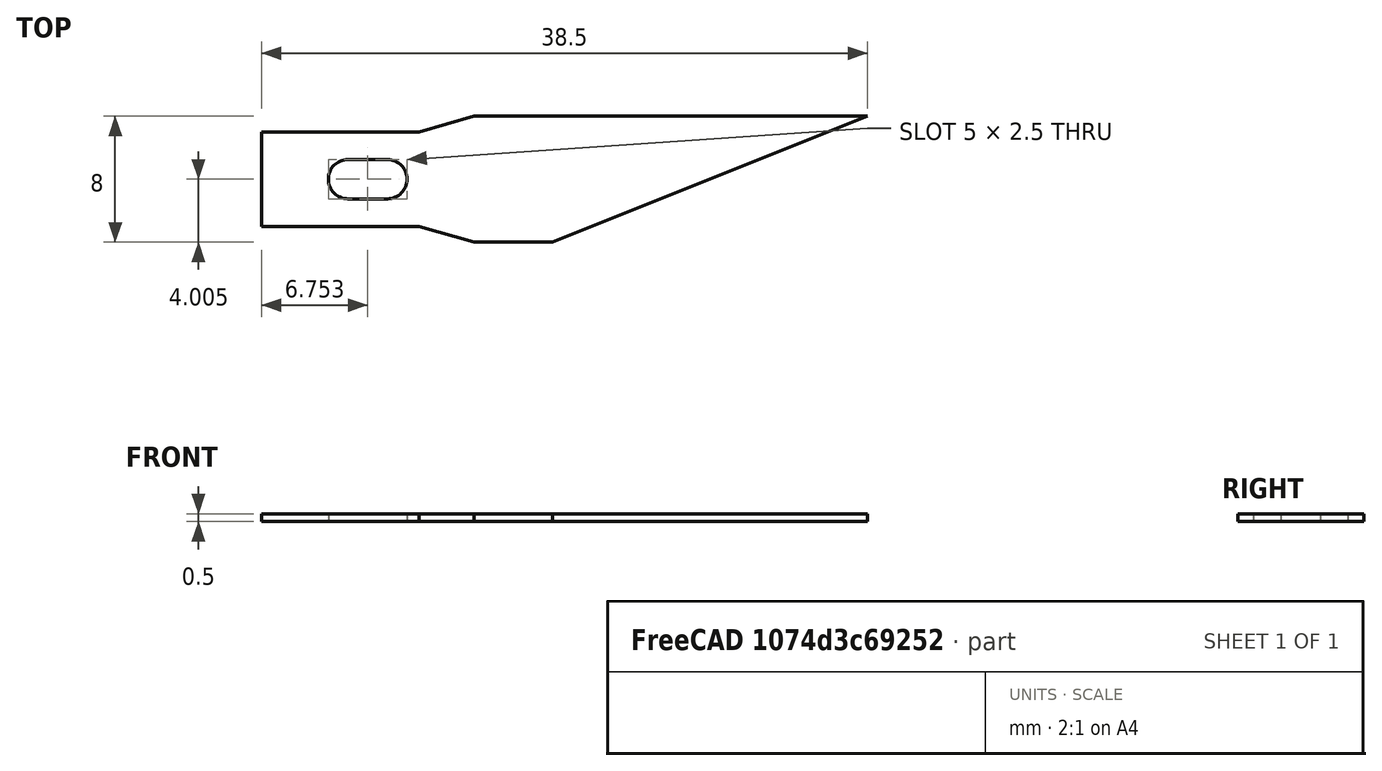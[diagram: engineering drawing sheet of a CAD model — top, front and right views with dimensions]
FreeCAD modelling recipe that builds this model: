
FCSTD DOCUMENT  (FreeCAD 0.19R24276 (Git))
Label: knife_holder_part_4
License: All rights reserved
LicenseURL: http://en.wikipedia.org/wiki/All_rights_reserved
objects: Sketcher::SketchObject×1, PartDesign::Pad×1, PartDesign::Body×1
note: 4 computed .brp shape members not serialized (recipe doc carries the construction recipe); baked Part::Feature solids carry a one-line shape summary decoded from their .brp

FEATURE [Sketcher::SketchObject] Sketch
  FullyConstrained = false
  MapMode = 5
  Support = -> [XY_Plane]
  sketch-geometry (29):
    g0: LineSegment StartX=-3.25677 StartY=9.76483 StartZ=0 EndX=35.2432 EndY=9.76483 EndZ=0
    g1: LineSegment StartX=35.2432 StartY=9.76483 StartZ=0 EndX=35.2432 EndY=1.76483 EndZ=0
    g2: LineSegment StartX=35.2432 StartY=1.76483 StartZ=0 EndX=-3.25677 EndY=1.76483 EndZ=0
    g3: LineSegment StartX=-3.25677 StartY=1.76483 StartZ=0 EndX=-3.25677 EndY=9.76483 EndZ=0
    g4: LineSegment StartX=-3.25677 StartY=1.76483 StartZ=0 EndX=10.2432 EndY=1.76483 EndZ=0
    g5: LineSegment StartX=10.2432 StartY=1.76483 StartZ=0 EndX=10.2432 EndY=8.76483 EndZ=0
    g6: LineSegment StartX=10.2432 StartY=8.76483 StartZ=0 EndX=-3.25677 EndY=8.76483 EndZ=0
    g7: LineSegment StartX=-3.25677 StartY=8.76483 StartZ=0 EndX=-3.25677 EndY=1.76483 EndZ=0
    g8: LineSegment StartX=-3.25677 StartY=8.76483 StartZ=0 EndX=6.74323 EndY=8.76483 EndZ=0
    g9: LineSegment StartX=6.74323 StartY=8.76483 StartZ=0 EndX=6.74323 EndY=2.76483 EndZ=0
    g10: LineSegment StartX=6.74323 StartY=2.76483 StartZ=0 EndX=-3.25677 EndY=2.76483 EndZ=0
    g11: LineSegment StartX=-3.25677 StartY=2.76483 StartZ=0 EndX=-3.25677 EndY=8.76483 EndZ=0
    g12: LineSegment StartX=15.2432 StartY=4.27418 StartZ=0 EndX=15.2432 EndY=1.76483 EndZ=0
    g13: LineSegment StartX=15.2432 StartY=1.76483 StartZ=0 EndX=35.2432 EndY=9.76483 EndZ=0
    g14: LineSegment StartX=10.2432 StartY=1.76483 StartZ=0 EndX=10.2432 EndY=9.76483 EndZ=0
    g15: LineSegment StartX=10.2432 StartY=1.76483 StartZ=0 EndX=6.74323 EndY=2.76483 EndZ=0
    g16: LineSegment StartX=6.74323 StartY=8.76483 StartZ=0 EndX=10.2432 EndY=9.76483 EndZ=0
    g17: ArcOfCircle CenterX=2.24323 CenterY=5.76483 CenterZ=0 NormalX=0 NormalY=0 NormalZ=1 AngleXU=0 Radius=1.25 StartAngle=1.5708 EndAngle=4.71239
    g18: ArcOfCircle CenterX=4.74323 CenterY=5.76483 CenterZ=0 NormalX=0 NormalY=0 NormalZ=1 AngleXU=0 Radius=1.25 StartAngle=4.71239 EndAngle=7.85398
    g19: LineSegment StartX=2.24323 StartY=4.51483 StartZ=0 EndX=4.74323 EndY=4.51483 EndZ=0
    g20: LineSegment StartX=2.24323 StartY=7.01483 StartZ=0 EndX=4.74323 EndY=7.01483 EndZ=0
    g21: LineSegment StartX=-3.25677 StartY=2.76483 StartZ=0 EndX=-3.25677 EndY=8.76483 EndZ=0
    g22: LineSegment StartX=-3.25677 StartY=8.76483 StartZ=0 EndX=6.74323 EndY=8.76483 EndZ=0
    g23: LineSegment StartX=6.74323 StartY=8.76483 StartZ=0 EndX=10.2432 EndY=9.76483 EndZ=0
    g24: LineSegment StartX=10.2432 StartY=9.76483 StartZ=0 EndX=35.2432 EndY=9.76483 EndZ=0
    g25: LineSegment StartX=35.2432 StartY=9.76483 StartZ=0 EndX=15.2432 EndY=1.76483 EndZ=0
    g26: LineSegment StartX=15.2432 StartY=1.76483 StartZ=0 EndX=10.2432 EndY=1.76483 EndZ=0
    g27: LineSegment StartX=10.2432 StartY=1.76483 StartZ=0 EndX=6.74323 EndY=2.76483 EndZ=0
    g28: LineSegment StartX=6.74323 StartY=2.76483 StartZ=0 EndX=-3.25677 EndY=2.76483 EndZ=0
  constraints (71):
    c: Coincident(g0,g1)
    c: Coincident(g1,g2)
    c: Coincident(g2,g3)
    c: Coincident(g3,g0)
    c: Horizontal(g0)
    c: Horizontal(g2)
    c: Vertical(g1)
    c: Vertical(g3)
    c: DistanceX(g2,g2) = 38.5
    c: DistanceY(g1,g1) = 8
    c: Coincident(g4,g5)
    c: Coincident(g5,g6)
    c: Coincident(g6,g7)
    c: Coincident(g7,g4)
    c: Horizontal(g4)
    c: Horizontal(g6)
    c: Vertical(g5)
    c: Vertical(g7)
    c: Coincident(g4,g2)
    c: DistanceX(g6,g6) = 13.5
    c: DistanceY(g6,g0) = 1
    c: Coincident(g8,g9)
    c: Coincident(g9,g10)
    c: Coincident(g10,g11)
    c: Coincident(g11,g8)
    c: Horizontal(g8)
    c: Horizontal(g10)
    c: Vertical(g9)
    c: Vertical(g11)
    c: Coincident(g8,g6)
    c: DistanceY(g10,g6) = 6
    c: DistanceX(g10,g10) = 10
    c: Vertical(g12)
    c: Horizontal(g12,g1)
    c: Coincident(g13,g12)
    c: Coincident(g13,g0)
    c: Vertical(g14)
    c: DistanceX(g14,g12) = 5
    c: Horizontal(g14,g12)
    c: DistanceX(g12,g1) = 20
    c: Coincident(g15,g4)
    c: Coincident(g15,g9)
    c: Horizontal(g14,g0)
    c: Coincident(g16,g8)
    c: Coincident(g16,g14)
    c: Tangent(g17,g20) = 1.5708
    c: Tangent(g17,g19) = -1.5708
    c: Tangent(g19,g18) = -1.5708
    c: Tangent(g20,g18) = 1.5708
    c: Horizontal(g19)
    c: Equal(g17,g18)
    c: Diameter(g18) = 2.5
    c: DistanceY(g10,g17) = 3
    c: DistanceX(g10,g17) = 5.5
    c: DistanceX(g17,g18) = 2.5
    c: Coincident(g21,g10)
    c: Coincident(g23,g8)
    c: Coincident(g24,g14)
    c: Coincident(g25,g0)
    c: Coincident(g26,g25)
    c: Coincident(g27,g26)
    c: Coincident(g28,g27)
    c: Coincident(g28,g21)
    c: Coincident(g21,g22)
    c: Coincident(g22,g23)
    c: Coincident(g23,g24)
    c: Coincident(g24,g25)
    c: Coincident(g25,g12)
    c: Coincident(g26,g4)
    c: Coincident(g27,g9)
    c: Coincident(g6,g21)
FEATURE [PartDesign::Pad] Pad
  Direction = (1,1,1)
  Length = 0.5
  Length2 = 100
  Profile = -> Sketch
  Type = 0
FEATURE [PartDesign::Body] Body
  Group = -> [Sketch,Pad]
  Origin = -> Origin
  Tip = -> Pad
